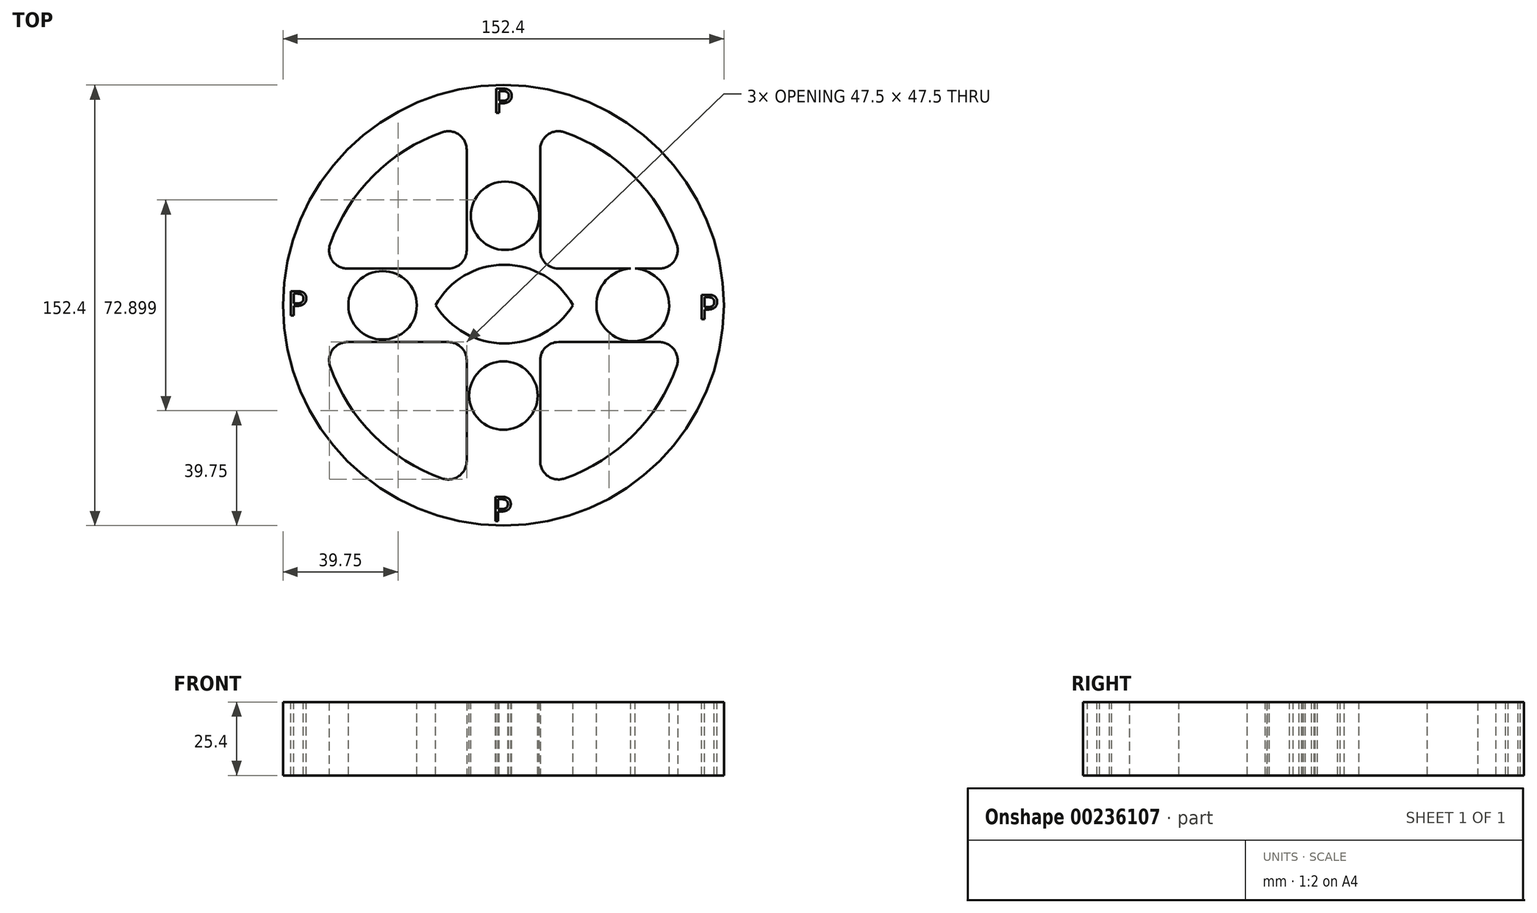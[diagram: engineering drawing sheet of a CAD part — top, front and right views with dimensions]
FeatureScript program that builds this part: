
annotation { "Feature Type Name" : "Feature", "Feature Type Description" : "" }
export const myFeature = defineFeature(function(context is Context, id is Id, definition is map)
    precondition{}
    {
        {
            var Q0;
            Q0=qCreatedBy(makeId("Top.planeOp"),FACE);
            var sketch = newSketch(context, id + "F0", { "sketchPlane" : qUnion([Q0])});
            skCircle(sketch, "E0", {"center": v(0, 0) * mm, "radius": 76.2 * mm});
            skArc(sketch, "E1", {"start": v(-21.17, 59.87) * mm, "mid": v(-44.9, 44.9) * mm, "end": v(-59.87, 21.17) * mm});
            skCircle(sketch, "E2", {"center": v(0, 0) * mm, "radius": 12.7 * mm});
            skLineSegment(sketch, "E3", {"start": v(0, 0) * mm, "end": v(0, 63.5) * mm});
            skLineSegment(sketch, "E4.0", {"start": v(12.7, 19.05) * mm, "end": v(12.7, 53.88) * mm});
            skLineSegment(sketch, "E5.0", {"start": v(-12.7, 19.05) * mm, "end": v(-12.7, 53.88) * mm});
            skLineSegment(sketch, "E6", {"start": v(0, 0) * mm, "end": v(0, -63.5) * mm});
            skLineSegment(sketch, "E7.0", {"start": v(-12.7, -19.05) * mm, "end": v(-12.7, -53.88) * mm});
            skLineSegment(sketch, "E8.0", {"start": v(12.7, -19.05) * mm, "end": v(12.7, -53.88) * mm});
            skLineSegment(sketch, "E9", {"start": v(0, 0) * mm, "end": v(-63.5, 0) * mm});
            skLineSegment(sketch, "E10.0", {"start": v(-19.05, 12.7) * mm, "end": v(-53.88, 12.7) * mm});
            skLineSegment(sketch, "E11.0", {"start": v(-19.05, -12.7) * mm, "end": v(-53.88, -12.7) * mm});
            skLineSegment(sketch, "E12", {"start": v(0, 0) * mm, "end": v(63.5, 0) * mm});
            skLineSegment(sketch, "E13.0", {"start": v(19.05, 12.7) * mm, "end": v(53.88, 12.7) * mm});
            skLineSegment(sketch, "E14.0", {"start": v(19.05, -12.7) * mm, "end": v(53.88, -12.7) * mm});
            skLineSegment(sketch, "E15.trimOffspring", {"start": v(-12.7, 75.13) * mm, "end": v(-12.7, 76.2) * mm});
            skLineSegment(sketch, "E16.trimOffspring", {"start": v(12.7, 75.13) * mm, "end": v(12.7, 76.2) * mm});
            skLineSegment(sketch, "E17.trimOffspring", {"start": v(75.13, 12.7) * mm, "end": v(76.2, 12.7) * mm});
            skLineSegment(sketch, "E18.trimOffspring", {"start": v(75.13, -12.7) * mm, "end": v(76.2, -12.7) * mm});
            skLineSegment(sketch, "E19.trimOffspring", {"start": v(12.7, -75.13) * mm, "end": v(12.7, -76.2) * mm});
            skLineSegment(sketch, "E20.trimOffspring", {"start": v(-12.7, -75.13) * mm, "end": v(-12.7, -76.2) * mm});
            skLineSegment(sketch, "E21.trimOffspring", {"start": v(-75.13, -12.7) * mm, "end": v(-76.2, -12.7) * mm});
            skLineSegment(sketch, "E22.trimOffspring", {"start": v(-75.13, 12.7) * mm, "end": v(-76.2, 12.7) * mm});
            skArc(sketch, "E23.trimOffspring", {"start": v(59.87, 21.17) * mm, "mid": v(44.9, 44.9) * mm, "end": v(21.17, 59.87) * mm});
            skArc(sketch, "E24.trimOffspring", {"start": v(21.17, -59.87) * mm, "mid": v(44.9, -44.9) * mm, "end": v(59.87, -21.17) * mm});
            skArc(sketch, "E25.trimOffspring", {"start": v(-59.87, -21.17) * mm, "mid": v(-44.9, -44.9) * mm, "end": v(-21.17, -59.87) * mm});
            skPoint(sketch, "E26.visualSharp", {"position": v(-12.7, 62.22) * mm});
            skArc(sketch, "E26.filletArc", {"start": v(-12.7, 53.88) * mm, "mid": v(-15.38, 59.07) * mm, "end": v(-21.17, 59.87) * mm});
            skPoint(sketch, "E27.visualSharp", {"position": v(-12.7, 12.7) * mm});
            skArc(sketch, "E27.filletArc", {"start": v(-19.05, 12.7) * mm, "mid": v(-14.56, 14.56) * mm, "end": v(-12.7, 19.05) * mm});
            skPoint(sketch, "E28.visualSharp", {"position": v(-62.22, 12.7) * mm});
            skArc(sketch, "E28.filletArc", {"start": v(-59.87, 21.17) * mm, "mid": v(-59.07, 15.38) * mm, "end": v(-53.88, 12.7) * mm});
            skPoint(sketch, "E29.visualSharp", {"position": v(12.7, 62.22) * mm});
            skArc(sketch, "E29.filletArc", {"start": v(21.17, 59.87) * mm, "mid": v(15.38, 59.07) * mm, "end": v(12.7, 53.88) * mm});
            skPoint(sketch, "E30.visualSharp", {"position": v(12.7, 12.7) * mm});
            skArc(sketch, "E30.filletArc", {"start": v(12.7, 19.05) * mm, "mid": v(14.56, 14.56) * mm, "end": v(19.05, 12.7) * mm});
            skPoint(sketch, "E31.visualSharp", {"position": v(62.22, 12.7) * mm});
            skArc(sketch, "E31.filletArc", {"start": v(53.88, 12.7) * mm, "mid": v(59.07, 15.38) * mm, "end": v(59.87, 21.17) * mm});
            skPoint(sketch, "E32.visualSharp", {"position": v(12.7, -12.7) * mm});
            skArc(sketch, "E32.filletArc", {"start": v(19.05, -12.7) * mm, "mid": v(14.56, -14.56) * mm, "end": v(12.7, -19.05) * mm});
            skPoint(sketch, "E33.visualSharp", {"position": v(62.22, -12.7) * mm});
            skArc(sketch, "E33.filletArc", {"start": v(59.87, -21.17) * mm, "mid": v(59.07, -15.38) * mm, "end": v(53.88, -12.7) * mm});
            skPoint(sketch, "E34.visualSharp", {"position": v(12.7, -62.22) * mm});
            skArc(sketch, "E34.filletArc", {"start": v(12.7, -53.88) * mm, "mid": v(15.38, -59.07) * mm, "end": v(21.17, -59.87) * mm});
            skPoint(sketch, "E35.visualSharp", {"position": v(-12.7, -62.22) * mm});
            skArc(sketch, "E35.filletArc", {"start": v(-21.17, -59.87) * mm, "mid": v(-15.38, -59.07) * mm, "end": v(-12.7, -53.88) * mm});
            skPoint(sketch, "E36.visualSharp", {"position": v(-12.7, -12.7) * mm});
            skArc(sketch, "E36.filletArc", {"start": v(-12.7, -19.05) * mm, "mid": v(-14.56, -14.56) * mm, "end": v(-19.05, -12.7) * mm});
            skPoint(sketch, "E37.visualSharp", {"position": v(-62.22, -12.7) * mm});
            skArc(sketch, "E37.filletArc", {"start": v(-53.88, -12.7) * mm, "mid": v(-59.07, -15.38) * mm, "end": v(-59.87, -21.17) * mm});
            skSolve(sketch);
        }
        {
            var Q0;
            Q0=makeQuery(id+"F0.imprint","IMPRINT",FACE,{"disambiguationData":[TD([[makeQuery(id+"F0.imprint","IMPRINT",EDGE,{"derivedFrom":sQuery(id+"F0.wireOp",EDGE,"E1")}),-1.0]])]});
            extrude(context, id + "F1", {"entities" : qUnion([Q0]), "endBound" : BoundingType.SYMMETRIC, "depth" : 25.4 * mm});
        }
        {
            var Q0;
            Q0=makeQuery(id+"F1.opExtrude","CAP_FACE",FACE,{"disambiguationData":[OSD([sQuery(id+"F0.wireOp",EDGE,"E0"),sQuery(id+"F0.wireOp",EDGE,"E1"),sQuery(id+"F0.wireOp",EDGE,"E2"),sQuery(id+"F0.wireOp",EDGE,"E4.0"),sQuery(id+"F0.wireOp",EDGE,"E5.0"),sQuery(id+"F0.wireOp",EDGE,"E7.0"),sQuery(id+"F0.wireOp",EDGE,"E8.0"),sQuery(id+"F0.wireOp",EDGE,"E10.0"),sQuery(id+"F0.wireOp",EDGE,"E11.0"),sQuery(id+"F0.wireOp",EDGE,"E13.0"),sQuery(id+"F0.wireOp",EDGE,"E14.0"),sQuery(id+"F0.wireOp",EDGE,"E23.trimOffspring"),sQuery(id+"F0.wireOp",EDGE,"E24.trimOffspring"),sQuery(id+"F0.wireOp",EDGE,"E25.trimOffspring")])],"isStart":false});
            var sketch = newSketch(context, id + "F2", { "sketchPlane" : qUnion([Q0])});
            skArc(sketch, "E38", {"start": v(24.06, 0) * mm, "mid": v(0.31, 14.06) * mm, "end": v(-23.44, 0) * mm});
            skArc(sketch, "E39", {"start": v(-23.44, 0) * mm, "mid": v(0.31, -13.18) * mm, "end": v(24.06, 0) * mm});
            skCircle(sketch, "E40", {"center": v(0, -31.22) * mm, "radius": 11.84 * mm});
            skCircle(sketch, "E41", {"center": v(0.57, 30.99) * mm, "radius": 11.84 * mm});
            skCircle(sketch, "E42", {"center": v(44.7, 0.15) * mm, "radius": 12.57 * mm});
            skCircle(sketch, "E43", {"center": v(-41.76, 0) * mm, "radius": 11.84 * mm});
            skText(sketch, "E44", { "text": "P\n", "fontName": "OpenSans-Regular.ttf"});
            skText(sketch, "E45", { "text": "P\n", "fontName": "OpenSans-Regular.ttf"});
            skText(sketch, "E46", { "text": "P\n", "fontName": "OpenSans-Regular.ttf"});
            skText(sketch, "E47", { "text": "P\n", "fontName": "OpenSans-Regular.ttf"});
            const initialGuessF2  = {"E44": [-0.00362, 0.06657, 1, 0, 0.00848], "E45": [0.0674, -0.00476, 1, 0, 0.00848], "E46": [-0.00393, -0.07463, 1, 0, 0.00848], "E47": [-0.07461, -0.00352, 1, 0, 0.00848]};
            skSetInitialGuess(sketch, initialGuessF2);
            skSolve(sketch);
        }
        {
            var Q0;
            Q0=makeQuery(id+"F2.imprint","IMPRINT",FACE,{"disambiguationData":[TD([[makeQuery(id+"F2.imprint","IMPRINT",EDGE,{"derivedFrom":sQuery(id+"F2.wireOp",EDGE,"E43")}),1.0]])]});
            var Q1;
            Q1=makeQuery(id+"F2.imprint","IMPRINT",FACE,{"disambiguationData":[TD([[makeQuery(id+"F2.imprint","IMPRINT",EDGE,{"derivedFrom":sQuery(id+"F2.wireOp",EDGE,"E40")}),1.0]])]});
            var Q2;
            Q2=makeQuery(id+"F2.imprint","IMPRINT",FACE,{"disambiguationData":[TD([[makeQuery(id+"F2.imprint","IMPRINT",EDGE,{"derivedFrom":sQuery(id+"F2.wireOp",EDGE,"E38")}),1.0]])]});
            var Q3;
            Q3=makeQuery(id+"F2.imprint","IMPRINT",FACE,{"disambiguationData":[TD([[makeQuery(id+"F2.imprint","IMPRINT",EDGE,{"derivedFrom":sQuery(id+"F2.wireOp",EDGE,"E42")}),1.0]])]});
            var Q4;
            Q4=makeQuery(id+"F2.imprint","IMPRINT",FACE,{"disambiguationData":[TD([[makeQuery(id+"F2.imprint","IMPRINT",EDGE,{"derivedFrom":sQuery(id+"F2.wireOp",EDGE,"E41")}),1.0]])]});
            extrude(context, id + "F3", {"entities" : qUnion([Q0, Q1, Q2, Q3, Q4]), "operationType" : NewBodyOperationType.REMOVE, "oppositeDirection" : true, "depth" : 77.47 * mm});
        }
        {
            var Q0;
            Q0=makeQuery(id+"F2.imprint","IMPRINT",FACE,{"disambiguationData":[TD([[makeQuery(id+"F2.imprint","IMPRINT",EDGE,{"derivedFrom":sQuery(id+"F2.wireOp",EDGE,"E47.sketch_text.stroke-0")}),-1.0]])]});
            var Q1;
            Q1=makeQuery(id+"F2.imprint","IMPRINT",FACE,{"disambiguationData":[TD([[makeQuery(id+"F2.imprint","IMPRINT",EDGE,{"derivedFrom":sQuery(id+"F2.wireOp",EDGE,"E45.sketch_text.stroke-0")}),-1.0]])]});
            var Q2;
            Q2=makeQuery(id+"F2.imprint","IMPRINT",FACE,{"disambiguationData":[TD([[makeQuery(id+"F2.imprint","IMPRINT",EDGE,{"derivedFrom":sQuery(id+"F2.wireOp",EDGE,"E44.sketch_text.stroke-0")}),-1.0]])]});
            var Q3;
            Q3=makeQuery(id+"F2.imprint","IMPRINT",FACE,{"disambiguationData":[TD([[makeQuery(id+"F2.imprint","IMPRINT",EDGE,{"derivedFrom":sQuery(id+"F2.wireOp",EDGE,"E46.sketch_text.stroke-0")}),-1.0]])]});
            extrude(context, id + "F4", {"entities" : qUnion([Q0, Q1, Q2, Q3]), "operationType" : NewBodyOperationType.REMOVE, "oppositeDirection" : true, "depth" : 87.88 * mm});
        }
    });
